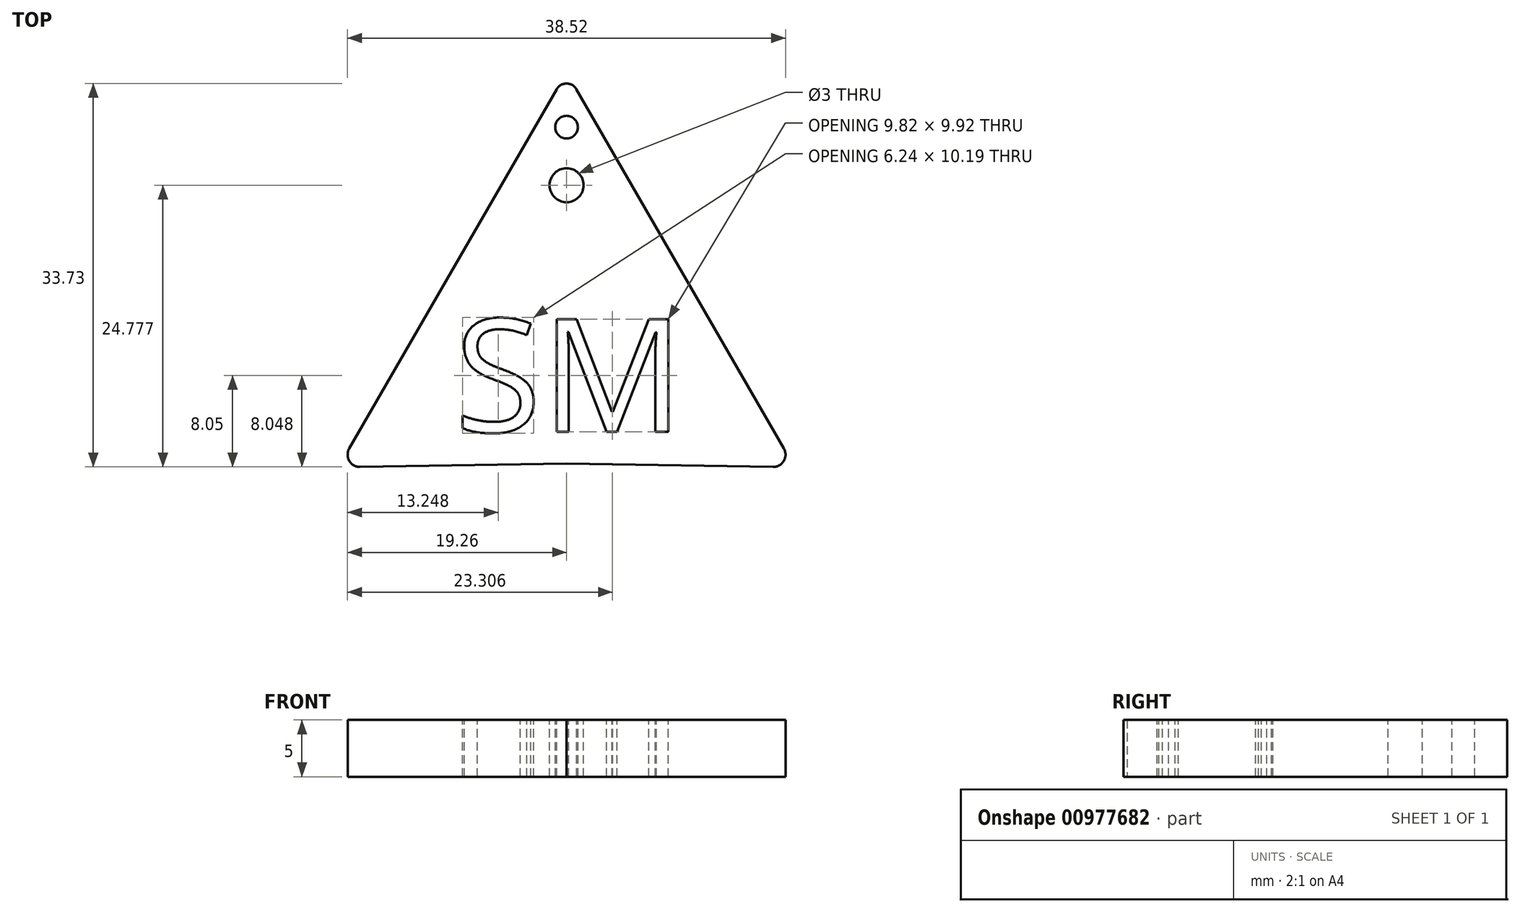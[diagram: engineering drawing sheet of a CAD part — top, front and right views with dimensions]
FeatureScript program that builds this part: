
annotation { "Feature Type Name" : "Feature", "Feature Type Description" : "" }
export const myFeature = defineFeature(function(context is Context, id is Id, definition is map)
    precondition{}
    {
        {
            var Q0;
            Q0=qCreatedBy(makeId("Top.planeOp"),FACE);
            var sketch = newSketch(context, id + "F0", { "sketchPlane" : qUnion([Q0])});
            skPoint(sketch, "E0.middle", {"position": v(0, 0) * mm});
            skLineSegment(sketch, "E1", {"start": v(-0.87, 15.82) * mm, "end": v(-19.11, -15.78) * mm});
            skPoint(sketch, "E2.orphan", {"position": v(-20, 17.32) * mm});
            skPoint(sketch, "E0.left.start.orphan", {"position": v(20, 17.32) * mm});
            skCircle(sketch, "E3", {"center": v(0, 15.32) * mm, "radius": 1 * mm});
            skPoint(sketch, "E4.orphan", {"position": v(0, 17.32) * mm});
            skLineSegment(sketch, "E5", {"start": v(-19.13, -16.84) * mm, "end": v(-17.22, -15.8) * mm});
            skCircle(sketch, "E6", {"center": v(-18.17, -16.33) * mm, "radius": 1.08 * mm});
            skLineSegment(sketch, "E7", {"start": v(-18.16, -17.41) * mm, "end": v(-18.2, -17.41) * mm});
            skLineSegment(sketch, "E8", {"start": v(-18.16, -17.41) * mm, "end": v(0, -17.1) * mm});
            skPoint(sketch, "E9.orphan", {"position": v(-20, -17.32) * mm});
            skPoint(sketch, "E10.orphan", {"position": v(-10.43, -0.75) * mm});
            skPoint(sketch, "E11.trimOffspring.end.orphan", {"position": v(10.43, -0.75) * mm});
            skPoint(sketch, "E12.orphan", {"position": v(20, -17.32) * mm});
            skPoint(sketch, "E13.end.orphan", {"position": v(0.87, 15.82) * mm});
            skLineSegment(sketch, "E14", {"start": v(0, 15.32) * mm, "end": v(0, 9.25) * mm});
            skLineSegment(sketch, "E15.MirrorCS", {"start": v(0.87, 15.82) * mm, "end": v(19.11, -15.78) * mm});
            skLineSegment(sketch, "E16.MirrorCS", {"start": v(18.16, -17.41) * mm, "end": v(0, -17.1) * mm});
            skCircle(sketch, "E17.MirrorC", {"center": v(18.17, -16.33) * mm, "radius": 1.08 * mm});
            skSolve(sketch);
        }
        {
            var Q0;
            Q0 = qSketchRegion(id + "F0", true);
            extrude(context, id + "F1", {"entities" : qUnion([Q0]), "depth" : 5 * mm, "offsetDistance" : 25 * mm});
        }
        {
            var Q0;
            Q0=makeQuery(id+"F1.opExtrude","CAP_FACE",FACE,{"disambiguationData":[OSD([sQuery(id+"F0.wireOp",EDGE,"E0.top"),sQuery(id+"F0.wireOp",EDGE,"E13"),sQuery(id+"F0.wireOp",EDGE,"E1")])],"isStart":false});
            var sketch = newSketch(context, id + "F2", { "sketchPlane" : qUnion([Q0])});
            skText(sketch, "E18", { "text": "SM", "fontName": "OpenSans-Regular.ttf"});
            const initialGuessF2  = {"E18": [-0.00985, -0.01432, 1, 0, 0.01]};
            skSetInitialGuess(sketch, initialGuessF2);
            skSolve(sketch);
        }
        {
            var Q0;
            Q0 = qSketchRegion(id + "F2", true);
            extrude(context, id + "F3", {"entities" : qUnion([Q0]), "operationType" : NewBodyOperationType.REMOVE, "endBound" : BoundingType.THROUGH_ALL, "oppositeDirection" : true, "depth" : 25 * mm, "offsetDistance" : 25 * mm});
        }
        {
            var Q0;
            Q0=makeQuery(id+"F1.opExtrude","CAP_FACE",FACE,{"disambiguationData":[OSD([sQuery(id+"F0.wireOp",EDGE,"E0.top"),sQuery(id+"F0.wireOp",EDGE,"E13"),sQuery(id+"F0.wireOp",EDGE,"E1")])],"isStart":false});
            var sketch = newSketch(context, id + "F4", { "sketchPlane" : qUnion([Q0])});
            skCircle(sketch, "E19", {"center": v(0, 12.48) * mm, "radius": 1 * mm});
            skCircle(sketch, "E20", {"center": v(0, 7.37) * mm, "radius": 1.5 * mm});
            skSolve(sketch);
        }
        {
            var Q0;
            Q0=makeQuery(id+"F4.imprint","IMPRINT",FACE,{"disambiguationData":[TD([[makeQuery(id+"F4.imprint","IMPRINT",EDGE,{"derivedFrom":sQuery(id+"F4.wireOp",EDGE,"E19")}),1.0]])]});
            var Q1;
            Q1=makeQuery(id+"F4.imprint","IMPRINT",FACE,{"disambiguationData":[TD([[makeQuery(id+"F4.imprint","IMPRINT",EDGE,{"derivedFrom":sQuery(id+"F4.wireOp",EDGE,"E20")}),1.0]])]});
            extrude(context, id + "F5", {"entities" : qUnion([Q0, Q1]), "operationType" : NewBodyOperationType.REMOVE, "endBound" : BoundingType.THROUGH_ALL, "oppositeDirection" : true, "depth" : 25 * mm, "offsetDistance" : 25 * mm});
        }
    });
